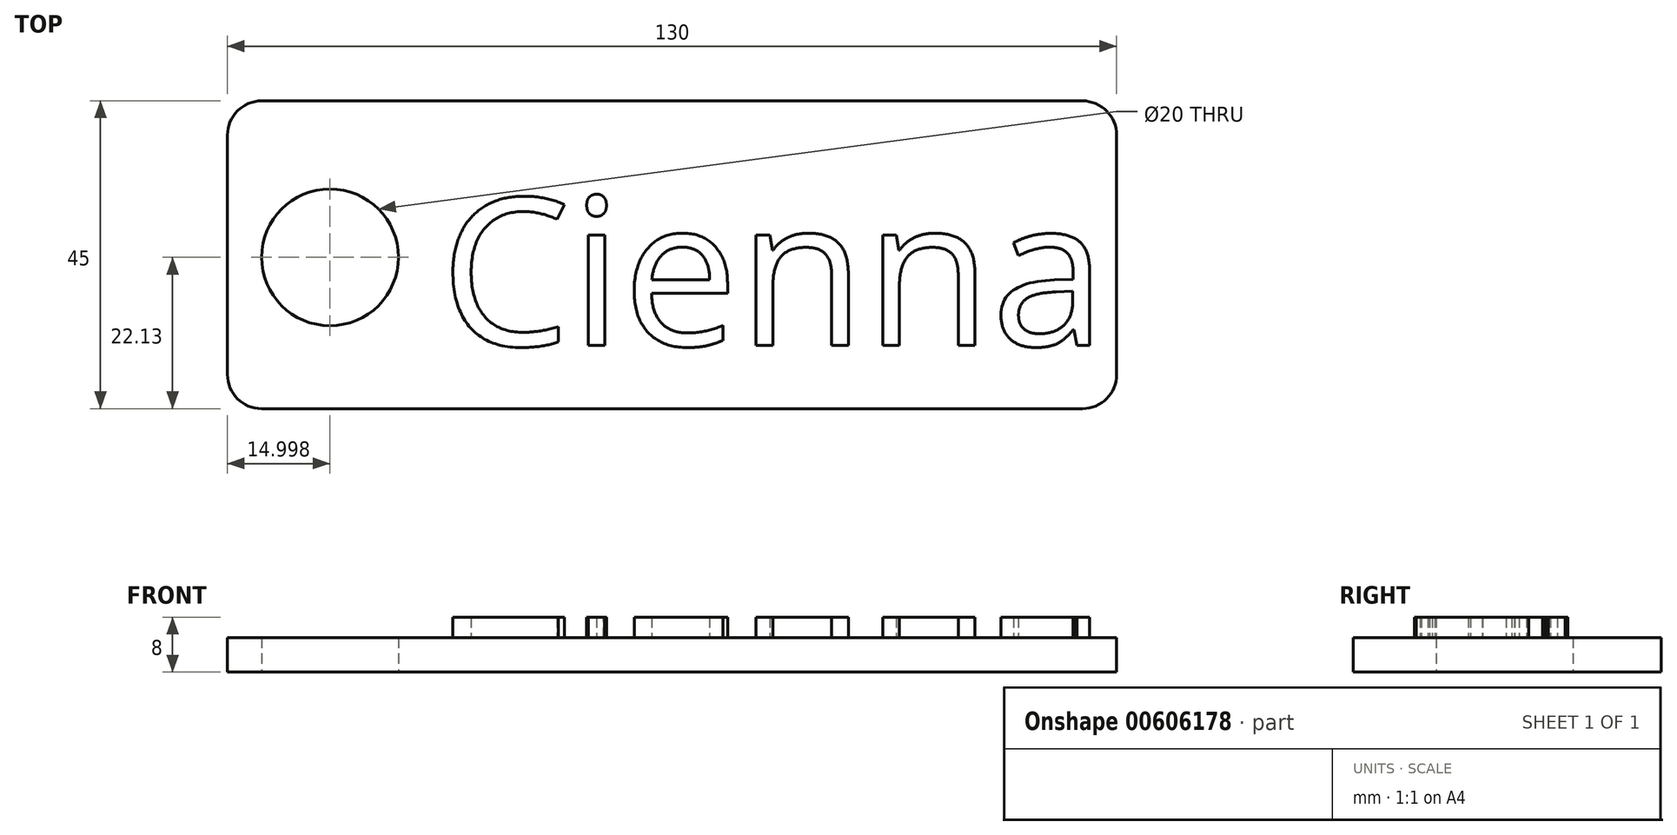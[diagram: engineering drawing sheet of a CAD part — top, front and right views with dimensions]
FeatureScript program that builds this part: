
annotation { "Feature Type Name" : "Feature", "Feature Type Description" : "" }
export const myFeature = defineFeature(function(context is Context, id is Id, definition is map)
    precondition{}
    {
        {
            var Q0;
            Q0=qCreatedBy(makeId("Top.planeOp"),FACE);
            var sketch = newSketch(context, id + "F0", { "sketchPlane" : qUnion([Q0])});
            skLineSegment(sketch, "E0.bottom", {"start": v(65.47, -22.13) * mm, "end": v(-64.53, -22.13) * mm});
            skLineSegment(sketch, "E0.top", {"start": v(65.47, 22.87) * mm, "end": v(-64.53, 22.87) * mm});
            skLineSegment(sketch, "E0.left", {"start": v(65.47, -22.13) * mm, "end": v(65.47, 22.87) * mm});
            skLineSegment(sketch, "E0.right", {"start": v(-64.53, -22.13) * mm, "end": v(-64.53, 22.87) * mm});
            skCircle(sketch, "E1", {"center": v(-49.53, 0) * mm, "radius": 10 * mm});
            skSolve(sketch);
        }
        {
            var Q0;
            Q0=makeQuery(id+"F0.imprint","IMPRINT",FACE,{"disambiguationData":[TD([[makeQuery(id+"F0.imprint","IMPRINT",EDGE,{"derivedFrom":sQuery(id+"F0.wireOp",EDGE,"E0.bottom")}),-1.0]])]});
            extrude(context, id + "F1", {"entities" : qUnion([Q0]), "depth" : 5 * mm, "offsetDistance" : 25 * mm});
        }
        {
            var Q0;
            Q0=makeQuery(id+"F1.opExtrude","CAP_FACE",FACE,{"disambiguationData":[OSD([sQuery(id+"F0.wireOp",EDGE,"E0.bottom"),sQuery(id+"F0.wireOp",EDGE,"E0.top"),sQuery(id+"F0.wireOp",EDGE,"E0.left"),sQuery(id+"F0.wireOp",EDGE,"E0.right"),sQuery(id+"F0.wireOp",EDGE,"E1")])],"isStart":false});
            var sketch = newSketch(context, id + "F2", { "sketchPlane" : qUnion([Q0])});
            skText(sketch, "E2", { "text": "Cienna", "fontName": "OpenSans-Regular.ttf"});
            const initialGuessF2  = {"E2": [-0.03341, -0.0129, 1, 0, 0.02171]};
            skSetInitialGuess(sketch, initialGuessF2);
            skSolve(sketch);
        }
        {
            var Q0;
            Q0 = qSketchRegion(id + "F2", true);
            var Q1;
            Q1 = qConstructionFilter(qBodyType(qCreatedBy(id + "F2" ,EDGE), BodyType.WIRE), ConstructionObject.NO);
            extrude(context, id + "F3", {"entities" : qUnion([Q0]), "operationType" : NewBodyOperationType.ADD, "surfaceEntities" : qUnion([Q1]), "depth" : 3 * mm, "offsetDistance" : 25 * mm});
        }
        {
            var Q0;
            Q0=makeQuery(id+"F1.opExtrude","SWEPT_EDGE",EDGE,{"disambiguationData":[OSD([sQuery(id+"F0.wireOp",EDGE,"E0.bottom"),sQuery(id+"F0.wireOp",EDGE,"E0.right")])]});
            var Q1;
            Q1=makeQuery(id+"F1.opExtrude","SWEPT_EDGE",EDGE,{"disambiguationData":[OSD([sQuery(id+"F0.wireOp",EDGE,"E0.bottom"),sQuery(id+"F0.wireOp",EDGE,"E0.left")])]});
            var Q2;
            Q2=makeQuery(id+"F1.opExtrude","SWEPT_EDGE",EDGE,{"disambiguationData":[OSD([sQuery(id+"F0.wireOp",EDGE,"E0.top"),sQuery(id+"F0.wireOp",EDGE,"E0.left")])]});
            var Q3;
            Q3=makeQuery(id+"F1.opExtrude","SWEPT_EDGE",EDGE,{"disambiguationData":[OSD([sQuery(id+"F0.wireOp",EDGE,"E0.top"),sQuery(id+"F0.wireOp",EDGE,"E0.right")])]});
            fillet(context, id + "F4", {"entities" : qUnion([Q0, Q1, Q2, Q3]), "radius" : 5 * mm, "tangentPropagation" : true, "allowEdgeOverflow" : false});
        }
    });
